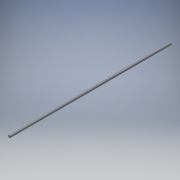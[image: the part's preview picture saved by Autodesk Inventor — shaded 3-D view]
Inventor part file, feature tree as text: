
AUTODESK INVENTOR PART (.ipt)
format: ipt  version: 2018 (Build 220112000, 112)  size: 92,160 bytes
history: native  units: in
note: dims shown in document units (in); Inventor stores cm internally (conversion verified against a paired STEP export)
features: revolve x1, sketch x1
ambient origin geometry x8: Origin, YZ Plane, XZ Plane, XY Plane, X Axis, Y Axis, Z Axis, Center Point
bodies: Solid1 (feature_tree)
feature tree (2):
  revolve  "Revolution1"  [1 undecoded]
  sketch  "Sketch1"  dims[d0=0.1575in d1=19.685in d2=90.0deg]
note: 1 required parameter value undecoded (feature->parameter linkage not recoverable at this tier; creation-order binding heuristic only, values carry confidence <= 0.55)
